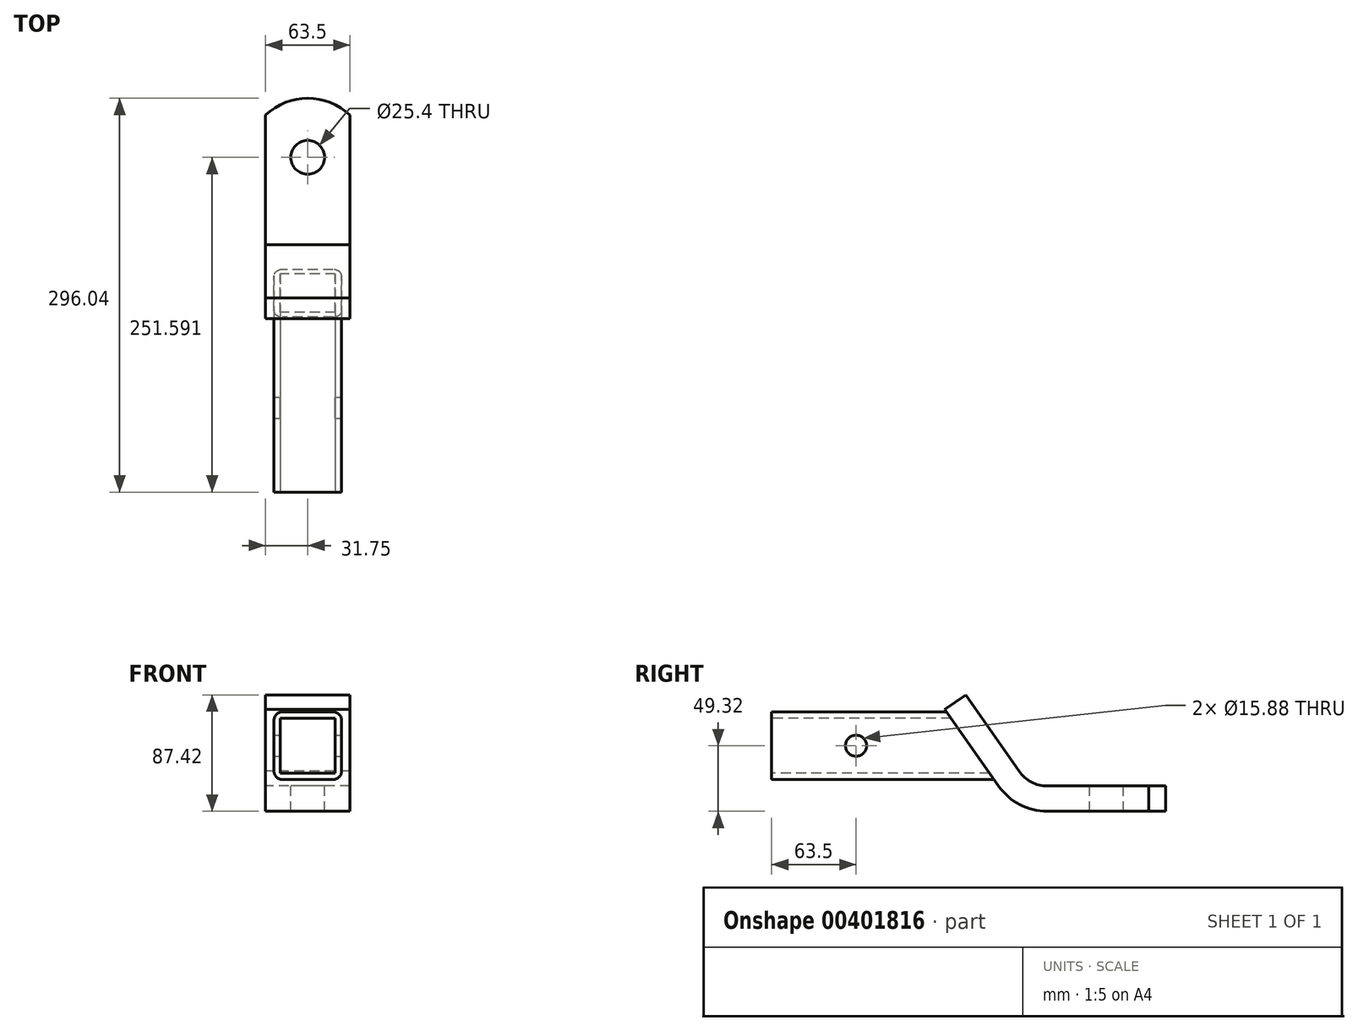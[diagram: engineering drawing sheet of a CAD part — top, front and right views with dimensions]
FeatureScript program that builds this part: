
annotation { "Feature Type Name" : "Feature", "Feature Type Description" : "" }
export const myFeature = defineFeature(function(context is Context, id is Id, definition is map)
    precondition{}
    {
        {
            var Q0;
            Q0=qCreatedBy(makeId("Front.planeOp"),FACE);
            var sketch = newSketch(context, id + "F0", { "sketchPlane" : qUnion([Q0])});
            skLineSegment(sketch, "E0.bottom", {"start": v(25.4, 25.4) * mm, "end": v(-25.4, 25.4) * mm});
            skLineSegment(sketch, "E0.top", {"start": v(25.4, -25.4) * mm, "end": v(-25.4, -25.4) * mm});
            skLineSegment(sketch, "E0.left", {"start": v(25.4, 25.4) * mm, "end": v(25.4, -25.4) * mm});
            skLineSegment(sketch, "E0.right", {"start": v(-25.4, 25.4) * mm, "end": v(-25.4, -25.4) * mm});
            skPoint(sketch, "E0.middle", {"position": v(0, 0) * mm});
            skLineSegment(sketch, "E1.bottom", {"start": v(20.62, 20.64) * mm, "end": v(-20.62, 20.64) * mm});
            skLineSegment(sketch, "E1.top", {"start": v(20.62, -20.64) * mm, "end": v(-20.62, -20.64) * mm});
            skLineSegment(sketch, "E1.left", {"start": v(20.62, 20.64) * mm, "end": v(20.62, -20.64) * mm});
            skLineSegment(sketch, "E1.right", {"start": v(-20.62, 20.64) * mm, "end": v(-20.62, -20.64) * mm});
            skSolve(sketch);
        }
        {
            var Q0;
            Q0=qCreatedBy(makeId("Right.planeOp"),FACE);
            var sketch = newSketch(context, id + "F1", { "sketchPlane" : qUnion([Q0])});
            skLineSegment(sketch, "E2", {"start": v(146.05, 38.1) * mm, "end": v(186.11, -19.12) * mm});
            skLineSegment(sketch, "E3", {"start": v(207.14, -30.27) * mm, "end": v(283.34, -30.27) * mm});
            skArc(sketch, "E4.filletArc", {"start": v(186.11, -19.12) * mm, "mid": v(195.24, -27.3) * mm, "end": v(207.14, -30.27) * mm});
            skLineSegment(sketch, "E5.0", {"start": v(130.28, 27.41) * mm, "end": v(170.5, -30.04) * mm});
            skLineSegment(sketch, "E6.0", {"start": v(207.14, -49.32) * mm, "end": v(283.34, -49.32) * mm});
            skArc(sketch, "E7.trimOffspring", {"start": v(170.5, -30.04) * mm, "mid": v(186.45, -44.2) * mm, "end": v(207.14, -49.32) * mm});
            skLineSegment(sketch, "E8", {"start": v(130.28, 27.41) * mm, "end": v(146.05, 38.1) * mm});
            skLineSegment(sketch, "E9", {"start": v(283.34, -30.27) * mm, "end": v(283.34, -49.32) * mm});
            skSolve(sketch);
        }
        {
            var Q0;
            Q0=makeQuery(id+"F1.imprint","IMPRINT",FACE,{"disambiguationData":[TD([[makeQuery(id+"F1.imprint","IMPRINT",EDGE,{"derivedFrom":sQuery(id+"F1.wireOp",EDGE,"E2")}),-1.0]])]});
            extrude(context, id + "F2", {"entities" : qUnion([Q0]), "endBound" : BoundingType.SYMMETRIC, "depth" : 63.5 * mm});
        }
        {
            var Q0;
            Q0=makeQuery(id+"F0.imprint","IMPRINT",FACE,{"disambiguationData":[TD([[makeQuery(id+"F0.imprint","IMPRINT",EDGE,{"derivedFrom":sQuery(id+"F0.wireOp",EDGE,"E0.bottom")}),1.0]])]});
            extrude(context, id + "F3", {"entities" : qUnion([Q0]), "endBound" : BoundingType.UP_TO_NEXT, "oppositeDirection" : true, "depth" : 25.4 * mm});
        }
        {
            var Q0;
            Q0=qCreatedBy(makeId("Right.planeOp"),FACE);
            var sketch = newSketch(context, id + "F4", { "sketchPlane" : qUnion([Q0])});
            skPoint(sketch, "E10", {"position": v(63.5, 0) * mm});
            skSolve(sketch);
        }
        {
            var Q0;
            Q0=qCreatedBy(makeId("Right.planeOp"),FACE);
            var sketch = newSketch(context, id + "F5", { "sketchPlane" : qUnion([Q0])});
            skCircle(sketch, "E11", {"center": v(63.5, 0) * mm, "radius": 7.94 * mm});
            skSolve(sketch);
        }
        {
            var Q0;
            Q0 = qSketchRegion(id + "F5", true);
            extrude(context, id + "F6", {"entities" : qUnion([Q0]), "operationType" : NewBodyOperationType.REMOVE, "endBound" : BoundingType.THROUGH_ALL, "oppositeDirection" : true, "depth" : 25.4 * mm, "hasSecondDirection" : true, "secondDirectionBound" : SecondDirectionBoundingType.THROUGH_ALL, "secondDirectionOppositeDirection" : false, "secondDirectionDepth" : 25.4 * mm});
        }
        {
            var Q0;
            Q0=makeQuery(id+"F2.opExtrude","SWEPT_FACE",FACE,{"disambiguationData":[OSD([sQuery(id+"F1.wireOp",EDGE,"E3")])]});
            var sketch = newSketch(context, id + "F7", { "sketchPlane" : qUnion([Q0])});
            skCircle(sketch, "E12", {"center": v(0, 251.6) * mm, "radius": 12.7 * mm});
            skSolve(sketch);
        }
        {
            var Q0;
            Q0=makeQuery(id+"F7.imprint","IMPRINT",FACE,{"disambiguationData":[TD([[makeQuery(id+"F7.imprint","IMPRINT",EDGE,{"derivedFrom":sQuery(id+"F7.wireOp",EDGE,"E12")}),1.0]])]});
            extrude(context, id + "F8", {"entities" : qUnion([Q0]), "operationType" : NewBodyOperationType.REMOVE, "endBound" : BoundingType.THROUGH_ALL, "oppositeDirection" : true, "depth" : 25.4 * mm});
        }
        {
            var Q0;
            Q0=makeQuery(id+"F2.opExtrude","SWEPT_FACE",FACE,{"disambiguationData":[OSD([sQuery(id+"F1.wireOp",EDGE,"E3")])]});
            var sketch = newSketch(context, id + "F9", { "sketchPlane" : qUnion([Q0])});
            skArc(sketch, "E13", {"start": v(31.75, 283.34) * mm, "mid": v(0, 296.04) * mm, "end": v(-31.75, 283.34) * mm});
            skSolve(sketch);
        }
        {
            var Q0;
            Q0=makeQuery(id+"F9.imprint","IMPRINT",FACE,{"disambiguationData":[TD([[makeQuery(id+"F9.imprint","IMPRINT",EDGE,{"derivedFrom":sQuery(id+"F9.wireOp",EDGE,"E13")}),1.0]])]});
            extrude(context, id + "F10", {"entities" : qUnion([Q0]), "operationType" : NewBodyOperationType.ADD, "oppositeDirection" : true, "depth" : 19.05 * mm});
        }
        {
            var Q0;
            Q0=makeQuery(id+"F3.opExtrude","SWEPT_EDGE",EDGE,{"disambiguationData":[OSD([sQuery(id+"F0.wireOp",EDGE,"E0.bottom"),sQuery(id+"F0.wireOp",EDGE,"E0.left")])]});
            var Q1;
            Q1=makeQuery(id+"F3.opExtrude","SWEPT_EDGE",EDGE,{"disambiguationData":[OSD([sQuery(id+"F0.wireOp",EDGE,"E0.bottom"),sQuery(id+"F0.wireOp",EDGE,"E0.right")])]});
            var Q2;
            Q2=makeQuery(id+"F3.opExtrude","SWEPT_EDGE",EDGE,{"disambiguationData":[OSD([sQuery(id+"F0.wireOp",EDGE,"E0.top"),sQuery(id+"F0.wireOp",EDGE,"E0.right")])]});
            var Q3;
            Q3=makeQuery(id+"F3.opExtrude","SWEPT_EDGE",EDGE,{"disambiguationData":[OSD([sQuery(id+"F0.wireOp",EDGE,"E0.top"),sQuery(id+"F0.wireOp",EDGE,"E0.left")])]});
            fillet(context, id + "F11", {"entities" : qUnion([Q0, Q1, Q2, Q3]), "radius" : 6.35 * mm, "tangentPropagation" : true, "allowEdgeOverflow" : false});
        }
    });
